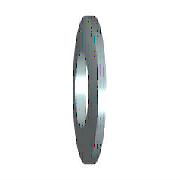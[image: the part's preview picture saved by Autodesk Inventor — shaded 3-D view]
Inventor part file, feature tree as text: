
AUTODESK INVENTOR PART (.ipt)
format: ipt  version: 2018 (Build 220112000, 112)  size: 117,248 bytes
history: native  units: mm (DEFAULTED — no unit token found)
features: other x2, plane x1
ambient origin geometry x7: Origin, YZ Plane, XY Plane, X Axis, Y Axis, Z Axis, Center Point
bodies: Solid1 (feature_tree)
feature tree (3):
  other  "IDS_BODY"
  other  "Work Axis1"
  plane  "Work Plane1"
